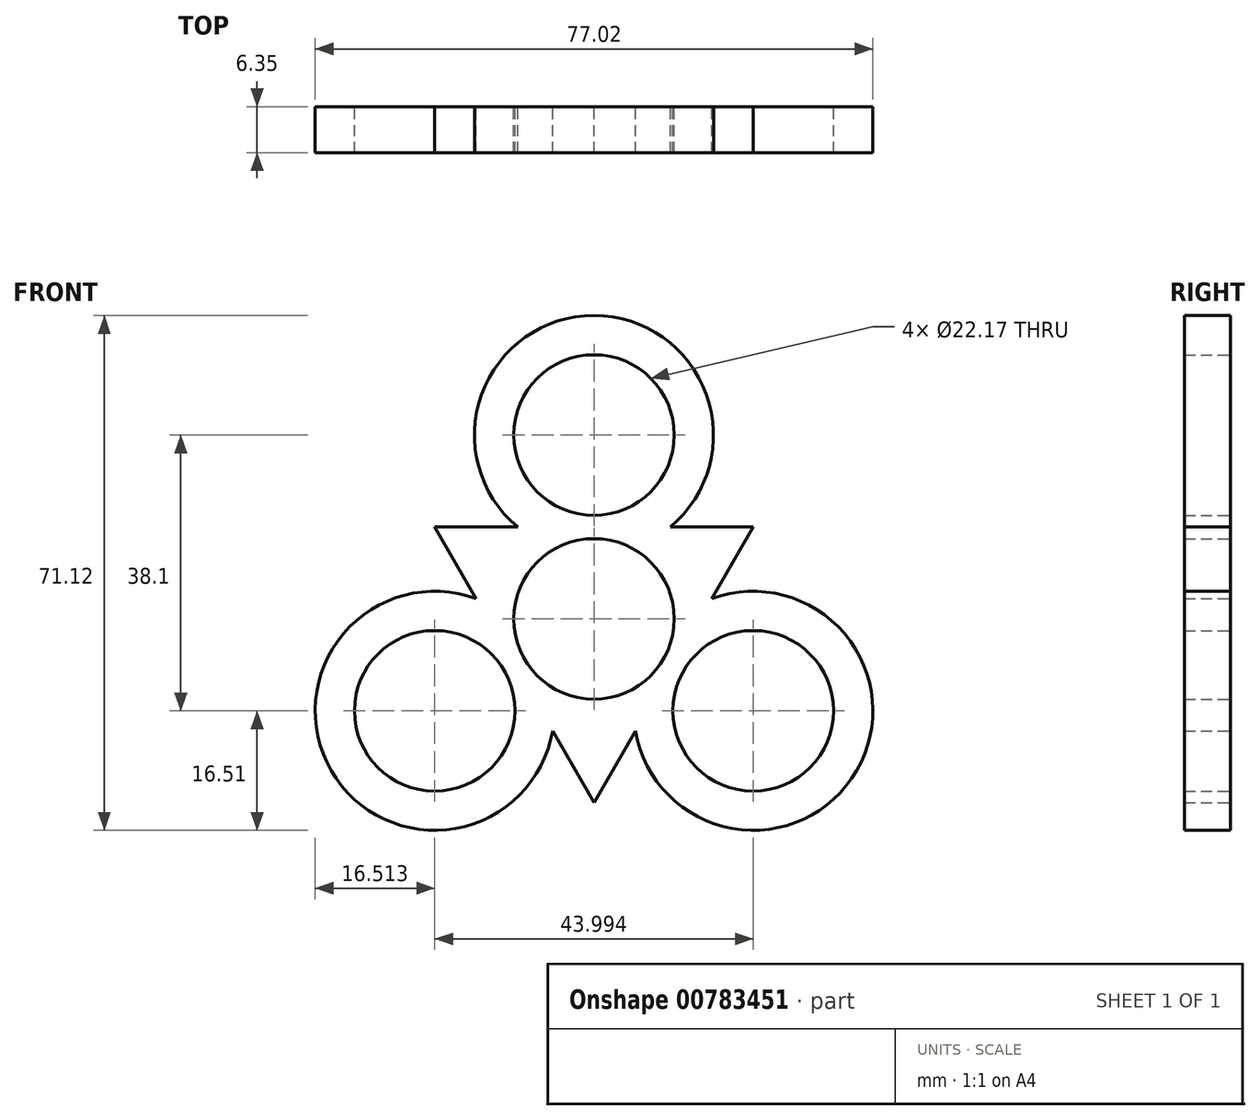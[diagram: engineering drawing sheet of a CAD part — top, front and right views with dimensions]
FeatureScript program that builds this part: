
annotation { "Feature Type Name" : "Feature", "Feature Type Description" : "" }
export const myFeature = defineFeature(function(context is Context, id is Id, definition is map)
    precondition{}
    {
        {
            var Q0;
            Q0=qCreatedBy(makeId("Front.planeOp"),FACE);
            var sketch = newSketch(context, id + "F0", { "sketchPlane" : qUnion([Q0])});
            skCircle(sketch, "E0", {"center": v(0, 0) * mm, "radius": 11.09 * mm});
            skLineSegment(sketch, "E1", {"start": v(0, 11.09) * mm, "end": v(0, 25.4) * mm});
            skLineSegment(sketch, "E2", {"start": v(9.6, -5.54) * mm, "end": v(22, -12.7) * mm});
            skLineSegment(sketch, "E3", {"start": v(-9.6, -5.54) * mm, "end": v(-22, -12.7) * mm});
            skCircle(sketch, "E4", {"center": v(22, -12.7) * mm, "radius": 11.09 * mm});
            skCircle(sketch, "E5", {"center": v(0, 25.4) * mm, "radius": 11.09 * mm});
            skCircle(sketch, "E6", {"center": v(-22, -12.7) * mm, "radius": 11.09 * mm});
            skArc(sketch, "E7", {"start": v(5.27, 9.75) * mm, "mid": v(0, 41.91) * mm, "end": v(-5.27, 9.75) * mm});
            skArc(sketch, "E8", {"start": v(5.81, -9.44) * mm, "mid": v(36.3, -20.96) * mm, "end": v(11.08, -0.31) * mm});
            skArc(sketch, "E9", {"start": v(-11.08, -0.31) * mm, "mid": v(-36.3, -20.95) * mm, "end": v(-5.81, -9.44) * mm});
            skLineSegment(sketch, "E10", {"start": v(-9.6, 5.54) * mm, "end": v(-22, 12.7) * mm});
            skLineSegment(sketch, "E11", {"start": v(9.6, 5.54) * mm, "end": v(22, 12.7) * mm});
            skLineSegment(sketch, "E12", {"start": v(0, 0) * mm, "end": v(0, -25.4) * mm});
            skLineSegment(sketch, "E13", {"start": v(-22, 12.7) * mm, "end": v(-10.55, 12.7) * mm});
            skLineSegment(sketch, "E14", {"start": v(-22, 12.7) * mm, "end": v(-16.27, 2.78) * mm});
            skLineSegment(sketch, "E15", {"start": v(0, -25.4) * mm, "end": v(-5.72, -15.49) * mm});
            skLineSegment(sketch, "E16", {"start": v(0, -25.4) * mm, "end": v(5.73, -15.5) * mm});
            skLineSegment(sketch, "E17", {"start": v(22, 12.7) * mm, "end": v(10.55, 12.7) * mm});
            skLineSegment(sketch, "E18", {"start": v(22, 12.7) * mm, "end": v(16.27, 2.78) * mm});
            skSolve(sketch);
        }
        {
            var Q0;
            Q0=makeQuery(id+"F0.imprint","IMPRINT",FACE,{"disambiguationData":[TD([[makeQuery(id+"F0.imprint","IMPRINT",EDGE,{"derivedFrom":sQuery(id+"F0.wireOp",EDGE,"E6")}),-1.0]])]});
            var Q1;
            Q1=makeQuery(id+"F0.imprint","IMPRINT",FACE,{"disambiguationData":[TD([[makeQuery(id+"F0.imprint","IMPRINT",EDGE,{"derivedFrom":sQuery(id+"F0.wireOp",EDGE,"E4")}),-1.0]])]});
            var Q2;
            Q2=makeQuery(id+"F0.imprint","IMPRINT",FACE,{"disambiguationData":[TD([[makeQuery(id+"F0.imprint","IMPRINT",EDGE,{"derivedFrom":sQuery(id+"F0.wireOp",EDGE,"E5")}),-1.0]])]});
            var Q3;
            {var subQ3=sQuery(id+"F0.wireOp",EDGE,"E11");Q3=makeQuery(id+"F0.imprint","IMPRINT",FACE,{"disambiguationData":[TD([[makeQuery(id+"F0.imprint","IMPRINT",EDGE,{"derivedFrom":subQ3}),1.0]])]});}
            var Q4;
            {var subQ3=sQuery(id+"F0.wireOp",EDGE,"E11");Q4=makeQuery(id+"F0.imprint","IMPRINT",FACE,{"disambiguationData":[TD([[makeQuery(id+"F0.imprint","IMPRINT",EDGE,{"derivedFrom":subQ3}),-1.0]])]});}
            var Q5;
            {var subQ5=sQuery(id+"F0.wireOp",EDGE,"E16");Q5=makeQuery(id+"F0.imprint","IMPRINT",FACE,{"disambiguationData":[TD([[makeQuery(id+"F0.imprint","IMPRINT",EDGE,{"derivedFrom":subQ5}),1.0]])]});}
            var Q6;
            {var subQ5=sQuery(id+"F0.wireOp",EDGE,"E15");Q6=makeQuery(id+"F0.imprint","IMPRINT",FACE,{"disambiguationData":[TD([[makeQuery(id+"F0.imprint","IMPRINT",EDGE,{"derivedFrom":subQ5}),-1.0]])]});}
            var Q7;
            {var subQ3=sQuery(id+"F0.wireOp",EDGE,"E10");Q7=makeQuery(id+"F0.imprint","IMPRINT",FACE,{"disambiguationData":[TD([[makeQuery(id+"F0.imprint","IMPRINT",EDGE,{"derivedFrom":subQ3}),1.0]])]});}
            var Q8;
            {var subQ3=sQuery(id+"F0.wireOp",EDGE,"E10");Q8=makeQuery(id+"F0.imprint","IMPRINT",FACE,{"disambiguationData":[TD([[makeQuery(id+"F0.imprint","IMPRINT",EDGE,{"derivedFrom":subQ3}),-1.0]])]});}
            extrude(context, id + "F1", {"entities" : qUnion([Q0, Q1, Q2, Q3, Q4, Q5, Q6, Q7, Q8]), "depth" : 6.35 * mm, "offsetDistance" : 25.4 * mm});
        }
    });
